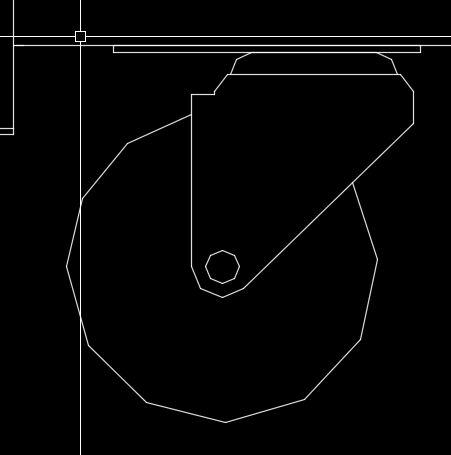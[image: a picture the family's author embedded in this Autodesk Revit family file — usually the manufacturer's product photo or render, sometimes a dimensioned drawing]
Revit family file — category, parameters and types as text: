
# Revit family: QF_EVEREST_ECB82D4
name_source: partatom
category: Specialty Equipment
revit_build: Autodesk Revit 2015 (Build: 20160512_0715(x64)
units: mm (PartAtom-declared; Revit-internal decimal feet)

## types (1)
- QF_EVEREST_ECB82D4
    Apparent Power = 288 VA
    BTUH = 2311.0 Btu/h
    Conn Conduit = Yes
    Conn Plug = NEMA 5-15P
    Cycle = 60 Hz
    Depth = 815 mm  [stored 2.67388 ft]
    Description = SIDE MOUNTED CONDENSING UNIT
    Elec Conn Connection Height = 0 mm  [stored 0 ft]
    Elec Conn RI Height = 0 mm  [stored 0 ft]
    FL Amps = 3 A
    Foodservice Equipment Identifier = Yes
    HP = 1/3
    Height = 635 mm
    Identify Quantity as Lot = Yes
    Length = 2091 mm  [stored 6.86024 ft]
    Manufacturer = EVEREST
    Max Overcurrent Protection = 0 A
    Min Ckt Ampacity = 0 A
    Model = ECB82D4
    Number of Poles = 1
    Phase = 1
    Refrigerant Type = R-290
    Refrigerant Volume = 0.00 kip
    Volts = 115 V
    Watts = 288 W
    Weight in Pounds = 484

note: [stored X ft] marks values corroborated as IEEE doubles in the binary element streams (Revit-internal decimal feet)

## geometry (parser evidence)
native form markers: Sweep x5
no freeform markers — native parametric forms only
